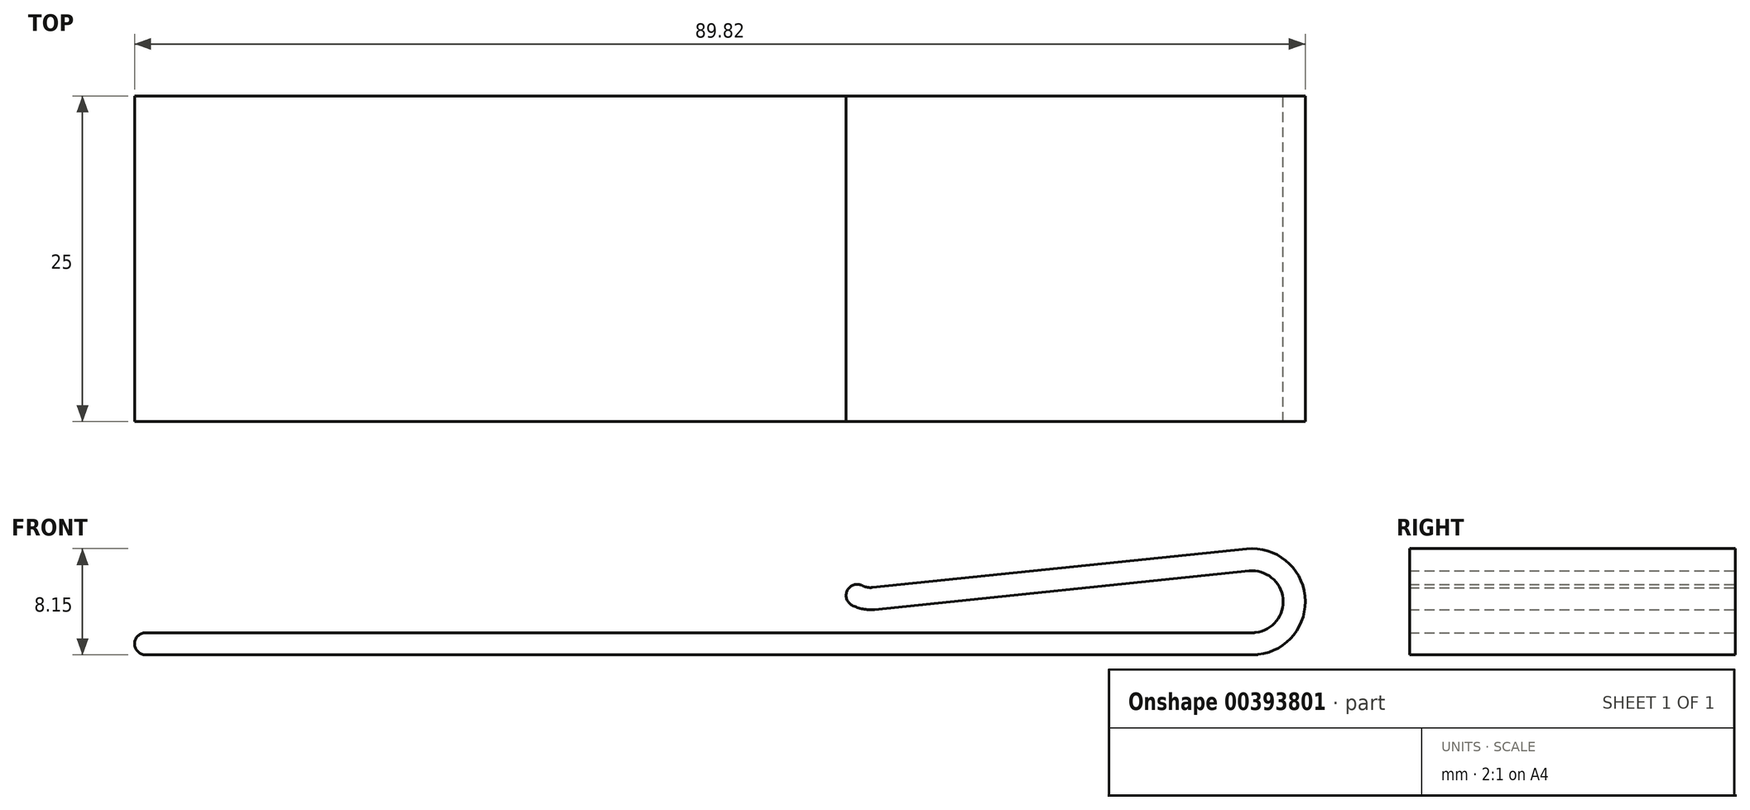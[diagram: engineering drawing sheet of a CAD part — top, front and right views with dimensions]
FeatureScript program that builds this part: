
annotation { "Feature Type Name" : "Feature", "Feature Type Description" : "" }
export const myFeature = defineFeature(function(context is Context, id is Id, definition is map)
    precondition{}
    {
        {
            var Q0;
            Q0=qCreatedBy(makeId("Front.planeOp"),FACE);
            var sketch = newSketch(context, id + "F0", { "sketchPlane" : qUnion([Q0])});
            skLineSegment(sketch, "E0", {"start": v(-39.15, 23.39) * mm, "end": v(45.79, 23.39) * mm});
            skLineSegment(sketch, "E1", {"start": v(16.78, 25.17) * mm, "end": v(45.5, 28.13) * mm});
            skArc(sketch, "E2", {"start": v(46.02, 23.4) * mm, "mid": v(48.1, 26.02) * mm, "end": v(45.5, 28.13) * mm});
            skPoint(sketch, "E3.visualSharp", {"position": v(45.85, 23.39) * mm});
            skArc(sketch, "E3.filletArc", {"start": v(45.79, 23.39) * mm, "mid": v(45.9, 23.4) * mm, "end": v(46.02, 23.4) * mm});
            skArc(sketch, "E4", {"start": v(15.04, 25.5) * mm, "mid": v(15.88, 25.2) * mm, "end": v(16.78, 25.17) * mm});
            skArc(sketch, "E5.0", {"start": v(15.83, 27) * mm, "mid": v(16.2, 26.87) * mm, "end": v(16.6, 26.86) * mm});
            skLineSegment(sketch, "E5.1", {"start": v(-39.15, 21.69) * mm, "end": v(45.79, 21.69) * mm});
            skArc(sketch, "E5.2", {"start": v(45.79, 21.69) * mm, "mid": v(46, 21.7) * mm, "end": v(46.22, 21.71) * mm});
            skArc(sketch, "E5.3", {"start": v(46.22, 21.71) * mm, "mid": v(49.8, 26.2) * mm, "end": v(45.32, 29.82) * mm});
            skLineSegment(sketch, "E5.4", {"start": v(16.6, 26.86) * mm, "end": v(45.32, 29.82) * mm});
            skArc(sketch, "E6", {"start": v(15.83, 27) * mm, "mid": v(14.68, 26.64) * mm, "end": v(15.04, 25.5) * mm});
            skArc(sketch, "E7", {"start": v(-39.15, 23.39) * mm, "mid": v(-40, 22.54) * mm, "end": v(-39.15, 21.69) * mm});
            skSolve(sketch);
        }
        {
            var Q0;
            Q0=qSketchRegion(id+"F0",true);
            extrude(context, id + "F1", {"entities" : qUnion([Q0]), "depth" : 25 * mm});
        }
    });
